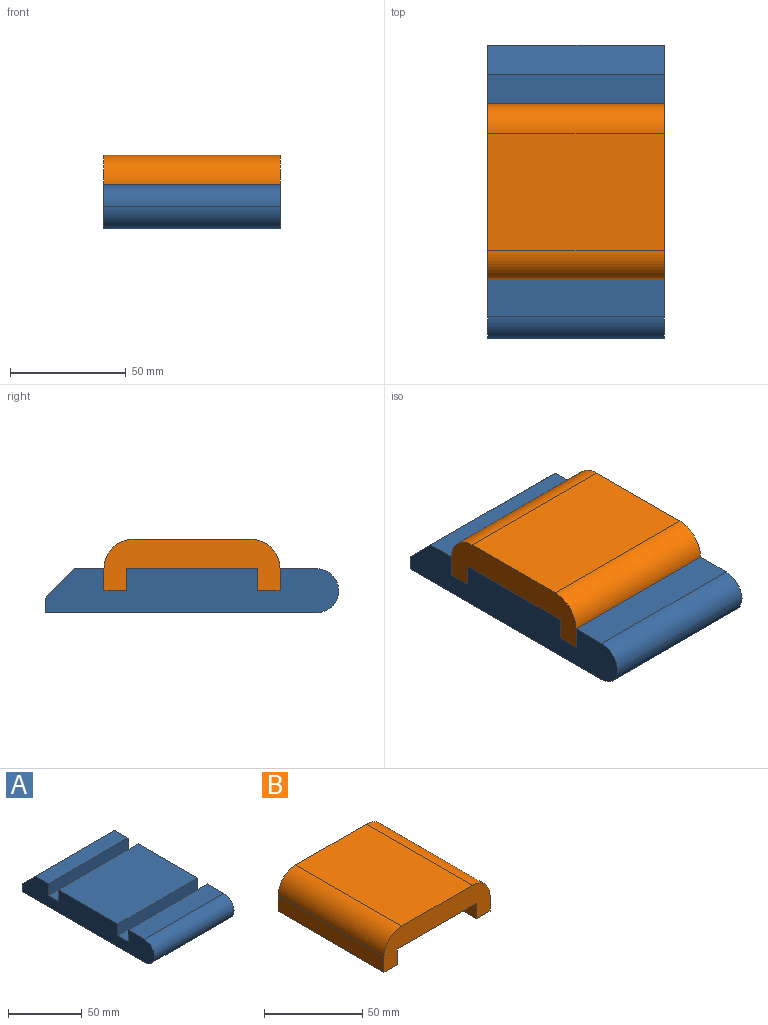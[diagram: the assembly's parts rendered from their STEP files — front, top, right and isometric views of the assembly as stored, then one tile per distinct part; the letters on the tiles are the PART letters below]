
ASSEMBLY  parts=2 mates=1
PART A: 16 faces, bbox 76.2x127x19.1 mm
  f0: plane 76.2x56.9mm, normal (0,0,1), area 4335.5mm2, adj f2,f3,f9,f11
  f1: plane 76.2x12.7mm, normal (0,0,1), area 967.7mm2, adj f2,f3,f7,f8
  f2: plane 127x19.05mm, normal (-1,0,0), area 2112.4mm2, adj f0,f1,f4,f5,f6,f7,f8,f9
  f3: plane 127x19.05mm, normal (1,0,0), area 2112.4mm2, adj f0,f1,f4,f5,f6,f7,f8,f9
  f4: plane 76.2x6.35mm, normal (0,1,0), area 483.9mm2, adj f2,f3,f6,f7
  f5: plane 76.2x15.75mm, normal (0,0,1), area 1200mm2, adj f2,f3,f12,f14
  f6: plane 117.35x76.2mm, normal (0,0,-1), area 8941.9mm2, adj f2,f3,f4,f15
  f7: plane 76.2x12.7mm, normal (0,0.71,0.71), area 1368.6mm2, adj f1,f2,f3,f4
  f8: plane 76.2x9.65mm, normal (0,-1,0), area 735.5mm2, adj f1,f2,f3,f10
  f9: plane 76.2x9.65mm, normal (0,1,0), area 735.5mm2, adj f0,f2,f3,f10
  f10: plane 76.2x9.65mm, normal (0,0,1), area 735.5mm2, adj f2,f3,f8,f9
  f11: plane 76.2x9.65mm, normal (0,-1,0), area 735.5mm2, adj f0,f2,f3,f13
  f12: plane 76.2x9.65mm, normal (0,1,0), area 735.5mm2, adj f2,f3,f5,f13
  f13: plane 76.2x9.65mm, normal (0,0,1), area 735.5mm2, adj f2,f3,f11,f12
  f14: cylinder r=9.65mm len=76.2mm, axis (-1,0,0), area 1145.6mm2, adj f2,f3,f5,f15
  f15: cylinder r=9.65mm len=76.2mm, axis (1,0,0), area 1145.6mm2, adj f2,f3,f6,f14
PART B: 12 faces, bbox 76.2x76.2x22.4 mm
  f0: plane 76.2x56.9mm, normal (0,0,-1), area 4335.5mm2, adj f2,f4,f6,f8
  f1: plane 76.2x9.65mm, normal (-1,0,0), area 735.5mm2, adj f2,f4,f7,f11
  f2: plane 76.2x22.35mm, normal (0,-1,0), area 1084.8mm2, adj f0,f1,f3,f5,f6,f7,f8,f9
  f3: plane 76.2x9.65mm, normal (1,0,0), area 735.5mm2, adj f2,f4,f9,f10
  f4: plane 76.2x22.35mm, normal (0,1,0), area 1084.8mm2, adj f0,f1,f3,f5,f6,f7,f8,f9
  f5: plane 76.2x50.8mm, normal (0,0,1), area 3871mm2, adj f2,f4,f10,f11
  f6: plane 76.2x9.65mm, normal (1,0,0), area 735.5mm2, adj f0,f2,f4,f7
  f7: plane 76.2x9.65mm, normal (0,0,-1), area 735.5mm2, adj f1,f2,f4,f6
  f8: plane 76.2x9.65mm, normal (-1,0,0), area 735.5mm2, adj f0,f2,f4,f9
  f9: plane 76.2x9.65mm, normal (0,0,-1), area 735.5mm2, adj f2,f3,f4,f8
  f10: cylinder r=12.7mm len=76.2mm, axis (0,-1,0), area 1520.1mm2, adj f2,f3,f4,f5
  f11: cylinder r=12.7mm len=76.2mm, axis (0,1,0), area 1520.1mm2, adj f1,f2,f4,f5
PLACE A at identity fixed
PLACE B rot(axis=(0,0,1),90deg) t=(0,0,19.05)mm
MATE slider A.f13 <-> B.f7  axis (0,0,1) through (0,-33.27,9.4)mm
